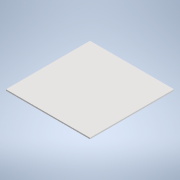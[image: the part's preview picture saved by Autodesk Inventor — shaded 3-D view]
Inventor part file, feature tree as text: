
AUTODESK INVENTOR PART (.ipt)
format: ipt  version: 2022 (Build 260153000, 153)  size: 90,112 bytes
history: native  units: mm
features: other x1, extrude x1, sketch x1
ambient origin geometry x8: Origin, YZ Plane, XZ Plane, XY Plane, X Axis, Y Axis, Z Axis, Center Point
bodies: Body1 (feature_tree)
feature tree (3):
  other  "Твердое тело1"
  extrude  "Выдавливание1"  Depth=200.0mm
  sketch  "Эскиз1"
